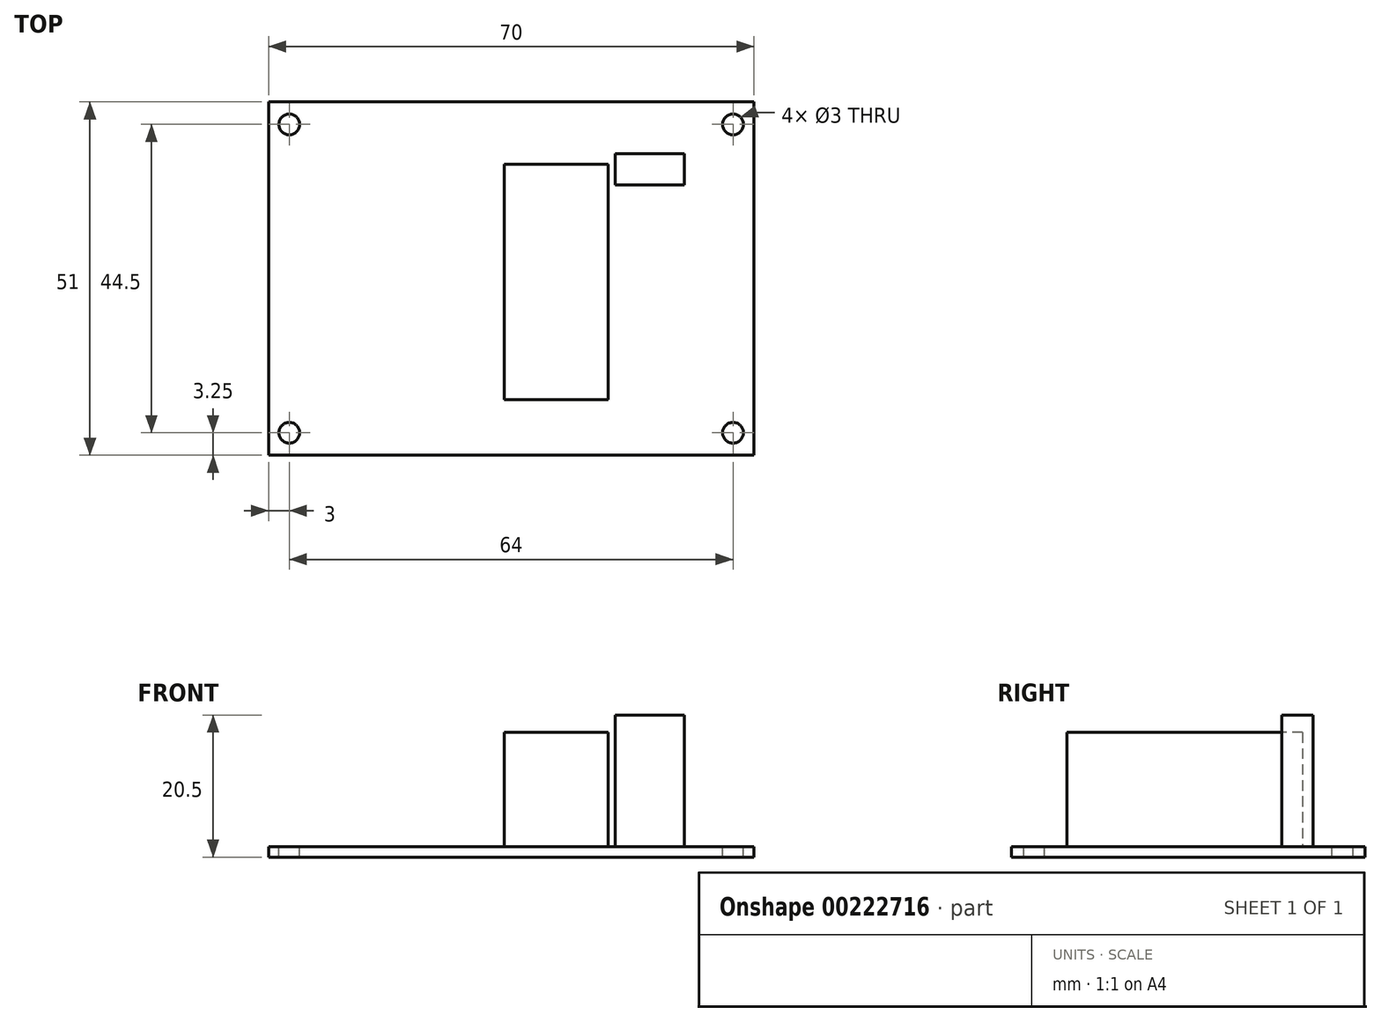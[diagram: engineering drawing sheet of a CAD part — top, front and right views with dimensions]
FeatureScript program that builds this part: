
annotation { "Feature Type Name" : "Feature", "Feature Type Description" : "" }
export const myFeature = defineFeature(function(context is Context, id is Id, definition is map)
    precondition{}
    {
        {
            var Q0;
            Q0=qCreatedBy(makeId("Top.planeOp"),FACE);
            var sketch = newSketch(context, id + "F0", { "sketchPlane" : qUnion([Q0])});
            skLineSegment(sketch, "E0.bottom", {"start": v(0, 0) * mm, "end": v(70, 0) * mm});
            skLineSegment(sketch, "E0.top", {"start": v(0, 51) * mm, "end": v(70, 51) * mm});
            skLineSegment(sketch, "E0.left", {"start": v(0, 0) * mm, "end": v(0, 51) * mm});
            skLineSegment(sketch, "E0.right", {"start": v(70, 0) * mm, "end": v(70, 51) * mm});
            skSolve(sketch);
        }
        {
            var Q0;
            Q0 = qSketchRegion(id + "F0", true);
            extrude(context, id + "F1", {"entities" : qUnion([Q0]), "depth" : 1.5 * mm});
        }
        {
            var Q0;
            Q0=makeQuery(id+"F1.opExtrude","CAP_FACE",FACE,{"disambiguationData":[OSD([sQuery(id+"F0.wireOp",EDGE,"E0.bottom"),sQuery(id+"F0.wireOp",EDGE,"E0.top"),sQuery(id+"F0.wireOp",EDGE,"E0.left"),sQuery(id+"F0.wireOp",EDGE,"E0.right")])],"isStart":false});
            var sketch = newSketch(context, id + "F2", { "sketchPlane" : qUnion([Q0])});
            skLineSegment(sketch, "E1.0.0", {"start": v(70, 51) * mm, "end": v(0, 51) * mm, "construction": true});
            skLineSegment(sketch, "E1.0.1", {"start": v(0, 51) * mm, "end": v(0, 0) * mm, "construction": true});
            skLineSegment(sketch, "E1.0.2", {"start": v(0, 0) * mm, "end": v(70, 0) * mm, "construction": true});
            skLineSegment(sketch, "E1.0.3", {"start": v(70, 0) * mm, "end": v(70, 51) * mm, "construction": true});
            skCircle(sketch, "E2", {"center": v(67, 47.75) * mm, "radius": 1.5 * mm});
            skCircle(sketch, "E3", {"center": v(67, 3.25) * mm, "radius": 1.5 * mm});
            skLineSegment(sketch, "E4.bottom", {"start": v(3, 3.25) * mm, "end": v(67, 3.25) * mm, "construction": true});
            skLineSegment(sketch, "E4.top", {"start": v(3, 47.75) * mm, "end": v(67, 47.75) * mm, "construction": true});
            skLineSegment(sketch, "E4.left", {"start": v(3, 3.25) * mm, "end": v(3, 47.75) * mm, "construction": true});
            skLineSegment(sketch, "E4.right", {"start": v(67, 3.25) * mm, "end": v(67, 47.75) * mm, "construction": true});
            skLineSegment(sketch, "E5", {"start": v(0, 25.5) * mm, "end": v(70, 25.5) * mm, "construction": true});
            skPoint(sketch, "E6", {"position": v(3, 25.5) * mm});
            skLineSegment(sketch, "E7", {"start": v(35, 51) * mm, "end": v(35, 0) * mm, "construction": true});
            skPoint(sketch, "E8", {"position": v(35, 47.75) * mm});
            skCircle(sketch, "E9", {"center": v(3, 47.75) * mm, "radius": 1.5 * mm});
            skCircle(sketch, "E10", {"center": v(3, 3.25) * mm, "radius": 1.5 * mm});
            skSolve(sketch);
        }
        {
            var Q0;
            Q0 = qSketchRegion(id + "F2", true);
            extrude(context, id + "F3", {"entities" : qUnion([Q0]), "operationType" : NewBodyOperationType.REMOVE, "endBound" : BoundingType.THROUGH_ALL, "oppositeDirection" : true, "depth" : 25 * mm});
        }
        {
            var Q0;
            Q0=makeQuery(id+"F1.opExtrude","CAP_FACE",FACE,{"disambiguationData":[OSD([sQuery(id+"F0.wireOp",EDGE,"E0.bottom"),sQuery(id+"F0.wireOp",EDGE,"E0.top"),sQuery(id+"F0.wireOp",EDGE,"E0.left"),sQuery(id+"F0.wireOp",EDGE,"E0.right")])],"isStart":false});
            var sketch = newSketch(context, id + "F4", { "sketchPlane" : qUnion([Q0])});
            skLineSegment(sketch, "E11.bottom", {"start": v(34, 42) * mm, "end": v(49, 42) * mm});
            skLineSegment(sketch, "E11.top", {"start": v(34, 8) * mm, "end": v(49, 8) * mm});
            skLineSegment(sketch, "E11.left", {"start": v(34, 42) * mm, "end": v(34, 8) * mm});
            skLineSegment(sketch, "E11.right", {"start": v(49, 42) * mm, "end": v(49, 8) * mm});
            skSolve(sketch);
        }
        {
            var Q0;
            Q0 = qSketchRegion(id + "F4", true);
            extrude(context, id + "F5", {"entities" : qUnion([Q0]), "operationType" : NewBodyOperationType.ADD, "depth" : 16.5 * mm});
        }
        {
            var Q0;
            Q0=makeQuery(id+"F1.opExtrude","CAP_FACE",FACE,{"disambiguationData":[OSD([sQuery(id+"F0.wireOp",EDGE,"E0.bottom"),sQuery(id+"F0.wireOp",EDGE,"E0.top"),sQuery(id+"F0.wireOp",EDGE,"E0.left"),sQuery(id+"F0.wireOp",EDGE,"E0.right")])],"isStart":false});
            var sketch = newSketch(context, id + "F6", { "sketchPlane" : qUnion([Q0])});
            skLineSegment(sketch, "E12.bottom", {"start": v(50, 43.5) * mm, "end": v(60, 43.5) * mm});
            skLineSegment(sketch, "E12.top", {"start": v(50, 39) * mm, "end": v(60, 39) * mm});
            skLineSegment(sketch, "E12.left", {"start": v(50, 43.5) * mm, "end": v(50, 39) * mm});
            skLineSegment(sketch, "E12.right", {"start": v(60, 43.5) * mm, "end": v(60, 39) * mm});
            skSolve(sketch);
        }
        {
            var Q0;
            Q0 = qSketchRegion(id + "F6", true);
            extrude(context, id + "F7", {"entities" : qUnion([Q0]), "operationType" : NewBodyOperationType.ADD, "depth" : 19 * mm});
        }
    });
